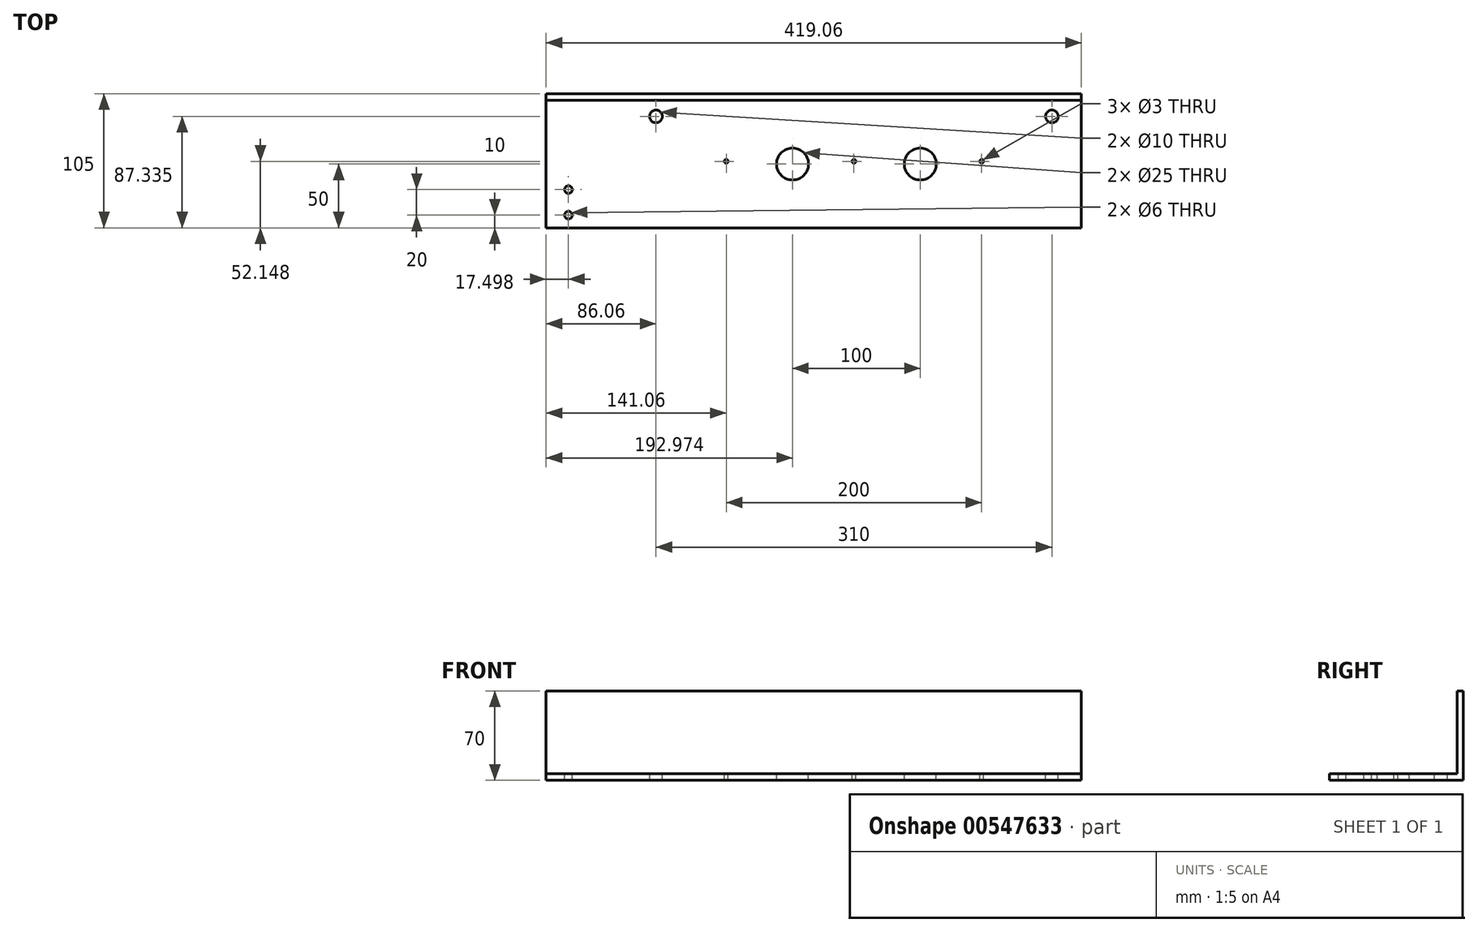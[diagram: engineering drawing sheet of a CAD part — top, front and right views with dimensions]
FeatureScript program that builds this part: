
annotation { "Feature Type Name" : "Feature", "Feature Type Description" : "" }
export const myFeature = defineFeature(function(context is Context, id is Id, definition is map)
    precondition{}
    {
        {
            var Q0;
            Q0=qCreatedBy(makeId("Top.planeOp"),FACE);
            var sketch = newSketch(context, id + "F0", { "sketchPlane" : qUnion([Q0])});
            skLineSegment(sketch, "E0.bottom", {"start": v(178, 50) * mm, "end": v(-178, 50) * mm});
            skLineSegment(sketch, "E0.top", {"start": v(178, -50) * mm, "end": v(-178, -50) * mm});
            skLineSegment(sketch, "E0.left", {"start": v(178, 50) * mm, "end": v(178, -50) * mm});
            skLineSegment(sketch, "E0.right", {"start": v(-178, 50) * mm, "end": v(-178, -50) * mm});
            skPoint(sketch, "E0.middle", {"position": v(0, 0) * mm});
            skSolve(sketch);
        }
        {
            var Q0;
            Q0=makeQuery(id+"F0.imprint","IMPRINT",FACE,{"disambiguationData":[TD([[makeQuery(id+"F0.imprint","IMPRINT",EDGE,{"derivedFrom":sQuery(id+"F0.wireOp",EDGE,"E0.bottom")}),1.0]])]});
            extrude(context, id + "F1", {"entities" : qUnion([Q0]), "depth" : 5 * mm, "offsetDistance" : 25 * mm});
        }
        {
            var Q0;
            Q0=makeQuery(id+"F1.opExtrude","CAP_FACE",FACE,{"disambiguationData":[OSD([sQuery(id+"F0.wireOp",EDGE,"E0.bottom"),sQuery(id+"F0.wireOp",EDGE,"E0.top"),sQuery(id+"F0.wireOp",EDGE,"E0.left"),sQuery(id+"F0.wireOp",EDGE,"E0.right")])],"isStart":false});
            var sketch = newSketch(context, id + "F2", { "sketchPlane" : qUnion([Q0])});
            skCircle(sketch, "E1", {"center": v(-155, 37.34) * mm, "radius": 5 * mm});
            skCircle(sketch, "E2", {"center": v(155, 37.34) * mm, "radius": 5 * mm});
            skLineSegment(sketch, "E3", {"start": v(-155, 37.34) * mm, "end": v(155, 37.34) * mm, "construction": true});
            skPoint(sketch, "E4", {"position": v(0, 37.34) * mm});
            skCircle(sketch, "E5", {"center": v(-48.09, 0) * mm, "radius": 12.5 * mm});
            skPoint(sketch, "E6", {"position": v(0, 0) * mm});
            skCircle(sketch, "E7", {"center": v(51.91, 0) * mm, "radius": 12.5 * mm});
            skSolve(sketch);
        }
        {
            var Q0;
            Q0=qSketchRegion(id+"F2",true);
            extrude(context, id + "F3", {"entities" : qUnion([Q0]), "operationType" : NewBodyOperationType.REMOVE, "endBound" : BoundingType.THROUGH_ALL, "oppositeDirection" : true, "depth" : 25 * mm, "offsetDistance" : 25 * mm});
        }
        {
            var Q0;
            Q0=makeQuery(id+"F1.opExtrude","CAP_FACE",FACE,{"disambiguationData":[OSD([sQuery(id+"F0.wireOp",EDGE,"E0.bottom"),sQuery(id+"F0.wireOp",EDGE,"E0.top"),sQuery(id+"F0.wireOp",EDGE,"E0.left"),sQuery(id+"F0.wireOp",EDGE,"E0.right")])],"isStart":false});
            var sketch = newSketch(context, id + "F4", { "sketchPlane" : qUnion([Q0])});
            skCircle(sketch, "E8", {"center": v(0, 2.15) * mm, "radius": 1.5 * mm});
            skCircle(sketch, "E9", {"center": v(100, 2.15) * mm, "radius": 1.5 * mm});
            skCircle(sketch, "E10", {"center": v(-100, 2.15) * mm, "radius": 1.5 * mm});
            skLineSegment(sketch, "E11", {"start": v(-100, 2.15) * mm, "end": v(0, 2.15) * mm, "construction": true});
            skLineSegment(sketch, "E12", {"start": v(0, 2.15) * mm, "end": v(100, 2.15) * mm, "construction": true});
            skSolve(sketch);
        }
        {
            var Q0;
            Q0=qSketchRegion(id+"F4",true);
            extrude(context, id + "F5", {"entities" : qUnion([Q0]), "operationType" : NewBodyOperationType.REMOVE, "endBound" : BoundingType.THROUGH_ALL, "oppositeDirection" : true, "depth" : 25 * mm, "offsetDistance" : 25 * mm});
        }
        {
            var Q0;
            Q0=qCreatedBy(makeId("Top.planeOp"),FACE);
            var sketch = newSketch(context, id + "F6", { "sketchPlane" : qUnion([Q0])});
            skLineSegment(sketch, "E13.bottom", {"start": v(61.73, 58.93) * mm, "end": v(12.32, 58.93) * mm});
            skLineSegment(sketch, "E13.top", {"start": v(61.73, 37.83) * mm, "end": v(12.32, 37.83) * mm});
            skLineSegment(sketch, "E13.left", {"start": v(61.73, 58.93) * mm, "end": v(61.73, 37.83) * mm});
            skLineSegment(sketch, "E13.right", {"start": v(12.32, 58.93) * mm, "end": v(12.32, 37.83) * mm});
            skPoint(sketch, "E13.middle", {"position": v(37.02, 48.38) * mm});
            skSolve(sketch);
        }
        {
            var Q0;
            Q0=qSketchRegion(id+"F6",true);
            extrude(context, id + "F7", {"entities" : qUnion([Q0]), "depth" : 25 * mm, "offsetDistance" : 25 * mm});
        }
        {
            var Q0;
            Q0=makeQuery(id+"F7.opExtrude","SWEPT_BODY",BODY,{"disambiguationData":[OSD([sQuery(id+"F6.wireOp",EDGE,"E13.bottom"),sQuery(id+"F6.wireOp",EDGE,"E13.top"),sQuery(id+"F6.wireOp",EDGE,"E13.left"),sQuery(id+"F6.wireOp",EDGE,"E13.right")])]});
            deleteBodies(context, id + "F8", {"entities" : qUnion([Q0])});
        }
        {
            var Q0;
            Q0=qCreatedBy(makeId("Top.planeOp"),FACE);
            var sketch = newSketch(context, id + "F9", { "sketchPlane" : qUnion([Q0])});
            skLineSegment(sketch, "E14.bottom", {"start": v(-178, 50) * mm, "end": v(-241.06, 50) * mm});
            skLineSegment(sketch, "E14.top", {"start": v(-178, -50) * mm, "end": v(-241.06, -50) * mm});
            skLineSegment(sketch, "E14.left", {"start": v(-178, 50) * mm, "end": v(-178, -50) * mm});
            skLineSegment(sketch, "E14.right", {"start": v(-241.06, 50) * mm, "end": v(-241.06, -50) * mm});
            skSolve(sketch);
        }
        {
            var Q0;
            Q0=qSketchRegion(id+"F9",true);
            var Q1;
            Q1=makeQuery(id+"F1.opExtrude","CAP_FACE",FACE,{"disambiguationData":[OSD([sQuery(id+"F0.wireOp",EDGE,"E0.bottom"),sQuery(id+"F0.wireOp",EDGE,"E0.top"),sQuery(id+"F0.wireOp",EDGE,"E0.left"),sQuery(id+"F0.wireOp",EDGE,"E0.right")])],"isStart":false});
            extrude(context, id + "F10", {"entities" : qUnion([Q0]), "operationType" : NewBodyOperationType.ADD, "endBound" : BoundingType.UP_TO_SURFACE, "depth" : 25 * mm, "endBoundEntityFace" : qUnion([Q1]), "offsetDistance" : 25 * mm});
        }
        {
            var Q0;
            {var subQ0=sQuery(id+"F0.wireOp",EDGE,"E0.right");var subQ1=sQuery(id+"F0.wireOp",EDGE,"E0.left");var subQ2=sQuery(id+"F0.wireOp",EDGE,"E0.top");var subQ3=sQuery(id+"F0.wireOp",EDGE,"E0.bottom");Q0=makeQuery(id+"F10.boolean.opBoolean","MERGE",FACE,{"derivedFrom":[makeQuery(id+"F1.opExtrude","CAP_FACE",FACE,{"disambiguationData":[OSD([subQ3,subQ2,subQ1,subQ0])],"isStart":false}),makeQuery(id+"F10.opExtrude","CAP_FACE",FACE,{"disambiguationData":[OSD([subQ3,subQ2,subQ1,subQ0])],"isStart":false})]});}
            var sketch = newSketch(context, id + "F11", { "sketchPlane" : qUnion([Q0])});
            skCircle(sketch, "E15", {"center": v(-223.56, -20) * mm, "radius": 3 * mm});
            skCircle(sketch, "E16", {"center": v(-223.56, -40) * mm, "radius": 3 * mm});
            skSolve(sketch);
        }
        {
            var Q0;
            Q0=qSketchRegion(id+"F11",true);
            extrude(context, id + "F12", {"entities" : qUnion([Q0]), "operationType" : NewBodyOperationType.REMOVE, "oppositeDirection" : true, "depth" : 25 * mm, "offsetDistance" : 25 * mm});
        }
        {
            var Q0;
            Q0=makeQuery(id+"F10.boolean.opBoolean","MERGE",FACE,{"derivedFrom":[makeQuery(id+"F1.opExtrude","CAP_FACE",FACE,{"disambiguationData":[OSD([sQuery(id+"F0.wireOp",EDGE,"E0.bottom"),sQuery(id+"F0.wireOp",EDGE,"E0.top"),sQuery(id+"F0.wireOp",EDGE,"E0.left"),sQuery(id+"F0.wireOp",EDGE,"E0.right")])],"isStart":true}),makeQuery(id+"F10.opExtrude","CAP_FACE",FACE,{"disambiguationData":[OSD([sQuery(id+"F9.wireOp",EDGE,"E14.bottom"),sQuery(id+"F9.wireOp",EDGE,"E14.top"),sQuery(id+"F9.wireOp",EDGE,"E14.left"),sQuery(id+"F9.wireOp",EDGE,"E14.right")])],"isStart":true})]});
            var sketch = newSketch(context, id + "F13", { "sketchPlane" : qUnion([Q0])});
            skLineSegment(sketch, "E17.bottom", {"start": v(178, -50) * mm, "end": v(-241.06, -50) * mm});
            skLineSegment(sketch, "E17.top", {"start": v(178, -55) * mm, "end": v(-241.06, -55) * mm});
            skLineSegment(sketch, "E17.left", {"start": v(178, -50) * mm, "end": v(178, -55) * mm});
            skLineSegment(sketch, "E17.right", {"start": v(-241.06, -50) * mm, "end": v(-241.06, -55) * mm});
            skSolve(sketch);
        }
        {
            var Q0;
            Q0 = qSketchRegion(id + "F13", true);
            extrude(context, id + "F14", {"entities" : qUnion([Q0]), "operationType" : NewBodyOperationType.ADD, "oppositeDirection" : true, "depth" : 70 * mm, "offsetDistance" : 25 * mm});
        }
    });
